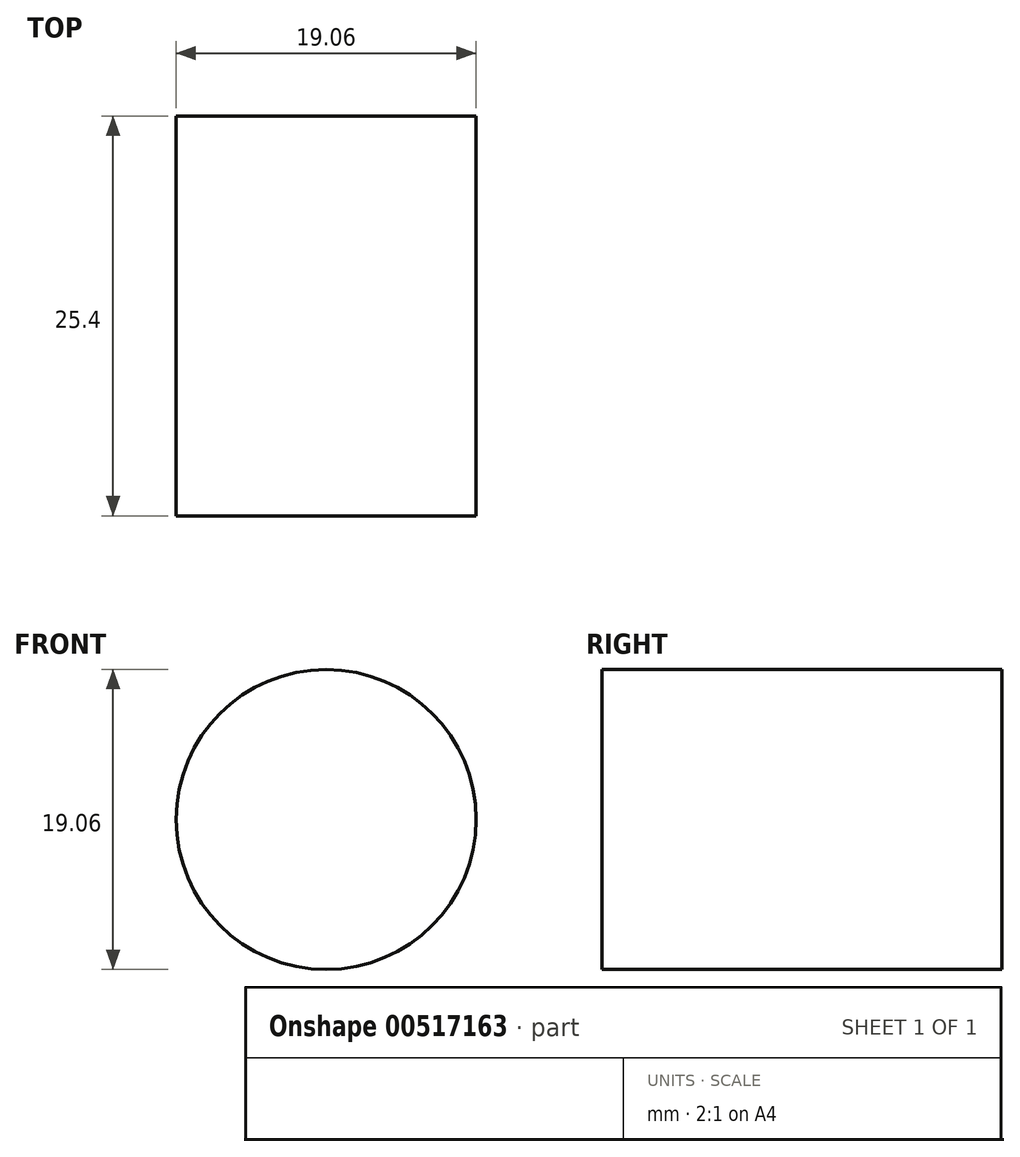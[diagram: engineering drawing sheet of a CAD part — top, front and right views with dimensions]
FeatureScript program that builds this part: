
annotation { "Feature Type Name" : "Feature", "Feature Type Description" : "" }
export const myFeature = defineFeature(function(context is Context, id is Id, definition is map)
    precondition{}
    {
        {
            var Q0;
            Q0=qCreatedBy(makeId("Front.planeOp"),FACE);
            var sketch = newSketch(context, id + "F0", { "sketchPlane" : qUnion([Q0])});
            skLineSegment(sketch, "E0", {"start": v(-70.36, 50.8) * mm, "end": v(-70.36, -63.5) * mm});
            skLineSegment(sketch, "E1", {"start": v(-70.36, 50.8) * mm, "end": v(-44.45, 50.8) * mm});
            skLineSegment(sketch, "E2", {"start": v(-44.45, 50.8) * mm, "end": v(-44.45, -63.5) * mm});
            skLineSegment(sketch, "E3", {"start": v(-70.36, -63.5) * mm, "end": v(-44.45, -63.5) * mm});
            skLineSegment(sketch, "E4", {"start": v(-44.45, 0) * mm, "end": v(-56.11, 0) * mm});
            skLineSegment(sketch, "E5", {"start": v(-56.11, 0) * mm, "end": v(-56.11, -63.5) * mm});
            skLineSegment(sketch, "E6", {"start": v(-56.11, -63.5) * mm, "end": v(-44.45, -63.5) * mm});
            skLineSegment(sketch, "E7", {"start": v(-44.45, -63.5) * mm, "end": v(0, -63.5) * mm});
            skLineSegment(sketch, "E8", {"start": v(0, -63.5) * mm, "end": v(0, -83.69) * mm});
            skLineSegment(sketch, "E9", {"start": v(0, -83.69) * mm, "end": v(-44.45, -83.69) * mm});
            skLineSegment(sketch, "E10", {"start": v(-44.45, -83.69) * mm, "end": v(-44.45, -63.5) * mm});
            skCircle(sketch, "E11", {"center": v(-44.45, 50.8) * mm, "radius": 14.86 * mm});
            skCircle(sketch, "E12", {"center": v(-44.45, 50.8) * mm, "radius": 9.53 * mm});
            skSolve(sketch);
        }
        {
            var Q0;
            Q0=sQuery(id+"F0.wireOp",EDGE,"E12");
            extrude(context, id + "F1", {"bodyType" : ToolBodyType.SURFACE, "surfaceEntities" : qUnion([Q0]), "depth" : 25.4 * mm, "offsetDistance" : 25.4 * mm});
        }
    });
